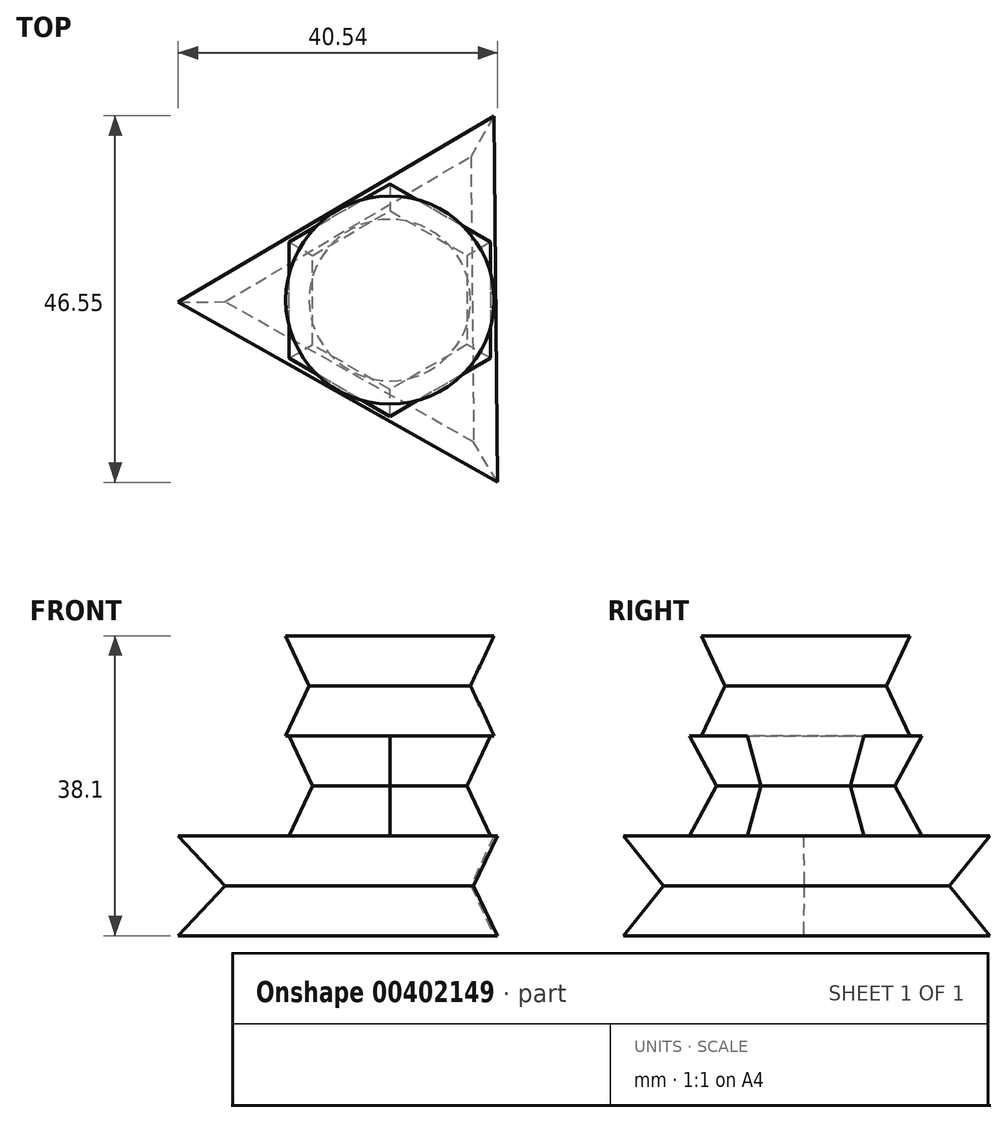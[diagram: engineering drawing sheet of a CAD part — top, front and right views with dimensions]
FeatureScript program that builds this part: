
annotation { "Feature Type Name" : "Feature", "Feature Type Description" : "" }
export const myFeature = defineFeature(function(context is Context, id is Id, definition is map)
    precondition{}
    {
        {
            var Q0;
            Q0=qCreatedBy(makeId("Top.planeOp"),FACE);
            cPlane(context, id + "F0", {"entities" : qUnion([Q0]), "cplaneType" : CPlaneType.OFFSET, "offset" : 12.7 * mm, "width" : 152.4 * mm, "height" : 152.4 * mm});
        }
        {
            var Q0;
            Q0=qCreatedBy(makeId("Top.planeOp"),FACE);
            cPlane(context, id + "F1", {"entities" : qUnion([Q0]), "cplaneType" : CPlaneType.OFFSET, "offset" : 25.4 * mm, "width" : 152.4 * mm, "height" : 152.4 * mm});
        }
        {
            var Q0;
            Q0=qCreatedBy(makeId("Top.planeOp"),FACE);
            var sketch = newSketch(context, id + "F2", { "sketchPlane" : qUnion([Q0])});
            skCircle(sketch, "E0.cCircle", {"center": v(0, 0) * mm, "radius": 10.48 * mm, "construction": true});
            skLineSegment(sketch, "E0.0", {"start": v(10.66, -18.04) * mm, "end": v(-20.95, -0.2) * mm});
            skLineSegment(sketch, "E0.1", {"start": v(-20.95, -0.2) * mm, "end": v(10.3, 18.25) * mm});
            skLineSegment(sketch, "E0.2", {"start": v(10.3, 18.25) * mm, "end": v(10.66, -18.04) * mm});
            skPoint(sketch, "E0.0.midPoint", {"position": v(-5.15, -9.12) * mm});
            skSolve(sketch);
        }
        {
            var Q0;
            Q0=qCreatedBy(id+"F0.planeOp",FACE);
            var sketch = newSketch(context, id + "F3", { "sketchPlane" : qUnion([Q0])});
            skCircle(sketch, "E1.cCircle", {"center": v(0, 0) * mm, "radius": 9.83 * mm, "construction": true});
            skLineSegment(sketch, "E1.0", {"start": v(-9.83, -5.67) * mm, "end": v(-9.83, 5.67) * mm});
            skLineSegment(sketch, "E1.1", {"start": v(-9.83, 5.67) * mm, "end": v(0, 11.35) * mm});
            skLineSegment(sketch, "E1.2", {"start": v(0, 11.35) * mm, "end": v(9.83, 5.67) * mm});
            skLineSegment(sketch, "E1.3", {"start": v(9.83, 5.67) * mm, "end": v(9.83, -5.67) * mm});
            skLineSegment(sketch, "E1.4", {"start": v(9.83, -5.67) * mm, "end": v(0, -11.35) * mm});
            skLineSegment(sketch, "E1.5", {"start": v(0, -11.35) * mm, "end": v(-9.83, -5.67) * mm});
            skPoint(sketch, "E1.0.midPoint", {"position": v(-9.83, 0) * mm});
            skSolve(sketch);
        }
        {
            var Q0;
            Q0=qCreatedBy(id+"F1.planeOp",FACE);
            var sketch = newSketch(context, id + "F4", { "sketchPlane" : qUnion([Q0])});
            skCircle(sketch, "E2", {"center": v(0, 0) * mm, "radius": 10.26 * mm});
            skSolve(sketch);
        }
        {
            var Q0;
            Q0 = qSketchRegion(id + "F2", true);
            var Q1;
            Q1 = qSketchRegion(id + "F4", true);
            var Q2;
            Q2 = qSketchRegion(id + "F3", true);
            extrude(context, id + "F5", {"entities" : qUnion([Q0, Q1, Q2]), "endBound" : BoundingType.SYMMETRIC, "depth" : 12.7 * mm, "hasDraft" : true, "draftAngle" : 25 * degree});
        }
    });
